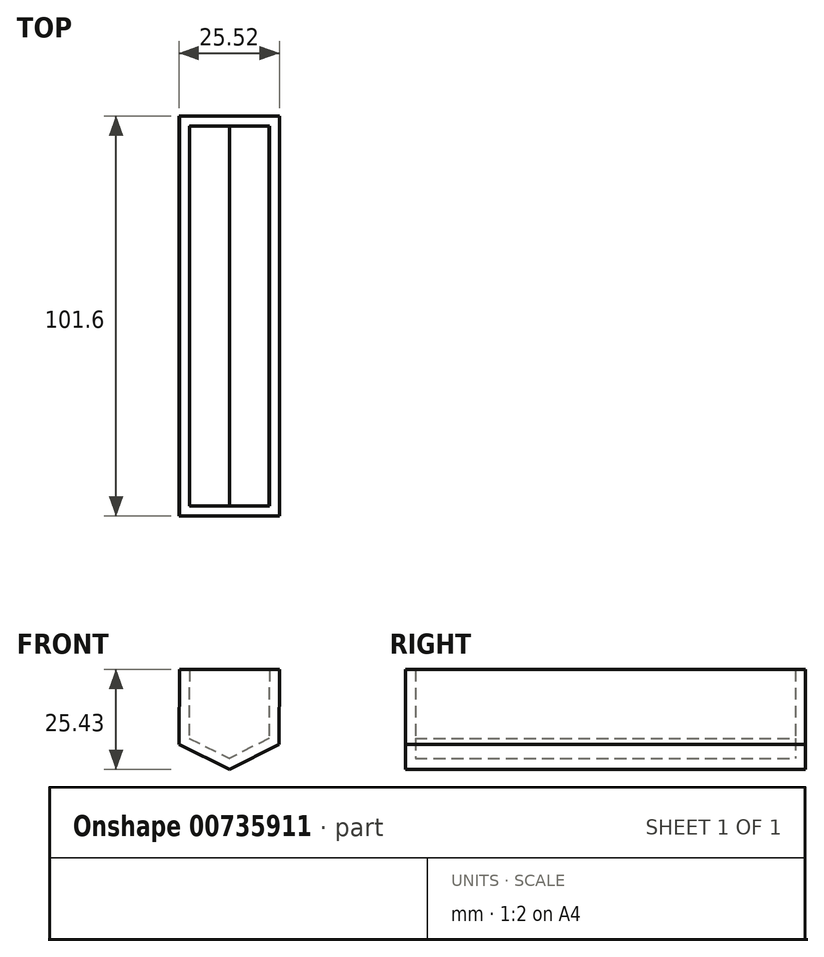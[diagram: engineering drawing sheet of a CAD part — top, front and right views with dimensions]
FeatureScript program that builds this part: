
annotation { "Feature Type Name" : "Feature", "Feature Type Description" : "" }
export const myFeature = defineFeature(function(context is Context, id is Id, definition is map)
    precondition{}
    {
        {
            var Q0;
            Q0=qCreatedBy(makeId("Front.planeOp"),FACE);
            var sketch = newSketch(context, id + "F0", { "sketchPlane" : qUnion([Q0])});
            skLineSegment(sketch, "E0", {"start": v(-56.3, 53.58) * mm, "end": v(-56.4, 34.53) * mm});
            skLineSegment(sketch, "E1", {"start": v(-30.9, 53.53) * mm, "end": v(-31, 34.48) * mm});
            skLineSegment(sketch, "E2", {"start": v(-56.3, 53.58) * mm, "end": v(-30.9, 53.53) * mm});
            skPoint(sketch, "E3.endSnap0", {"position": v(-43.7, 34.5) * mm});
            skLineSegment(sketch, "E4", {"start": v(-56.3, 53.58) * mm, "end": v(-43.6, 53.55) * mm});
            skLineSegment(sketch, "E5", {"start": v(-56.4, 34.53) * mm, "end": v(-43.6, 28.15) * mm});
            skLineSegment(sketch, "E6", {"start": v(-31, 34.48) * mm, "end": v(-43.6, 28.15) * mm});
            skSolve(sketch);
        }
        {
            var Q0;
            Q0=makeQuery(id+"F0.imprint","IMPRINT",FACE,{"disambiguationData":[TD([[makeQuery(id+"F0.imprint","IMPRINT",EDGE,{"derivedFrom":sQuery(id+"F0.wireOp",EDGE,"E0")}),1.0]])]});
            extrude(context, id + "F1", {"entities" : qUnion([Q0]), "depth" : 101.6 * mm, "offsetDistance" : 25.4 * mm});
        }
        {
            var Q0;
            Q0=makeQuery(id+"F1.opExtrude","SWEPT_FACE",FACE,{"disambiguationData":[OSD([sQuery(id+"F0.wireOp",EDGE,"E2"),sQuery(id+"F0.wireOp",EDGE,"E4")])]});
            var Q1;
            Q1=makeQuery(id+"F1.opExtrude","SWEPT_BODY",BODY,{"disambiguationData":[OSD([sQuery(id+"F0.wireOp",EDGE,"E0"),sQuery(id+"F0.wireOp",EDGE,"E1"),sQuery(id+"F0.wireOp",EDGE,"E2"),sQuery(id+"F0.wireOp",EDGE,"E4"),sQuery(id+"F0.wireOp",EDGE,"E5"),sQuery(id+"F0.wireOp",EDGE,"E6")])]});
            shell(context, id + "F2", {"entities" : qUnion([Q0]), "parts" : qUnion([Q1]), "thickness" : 2.54 * mm});
        }
    });
